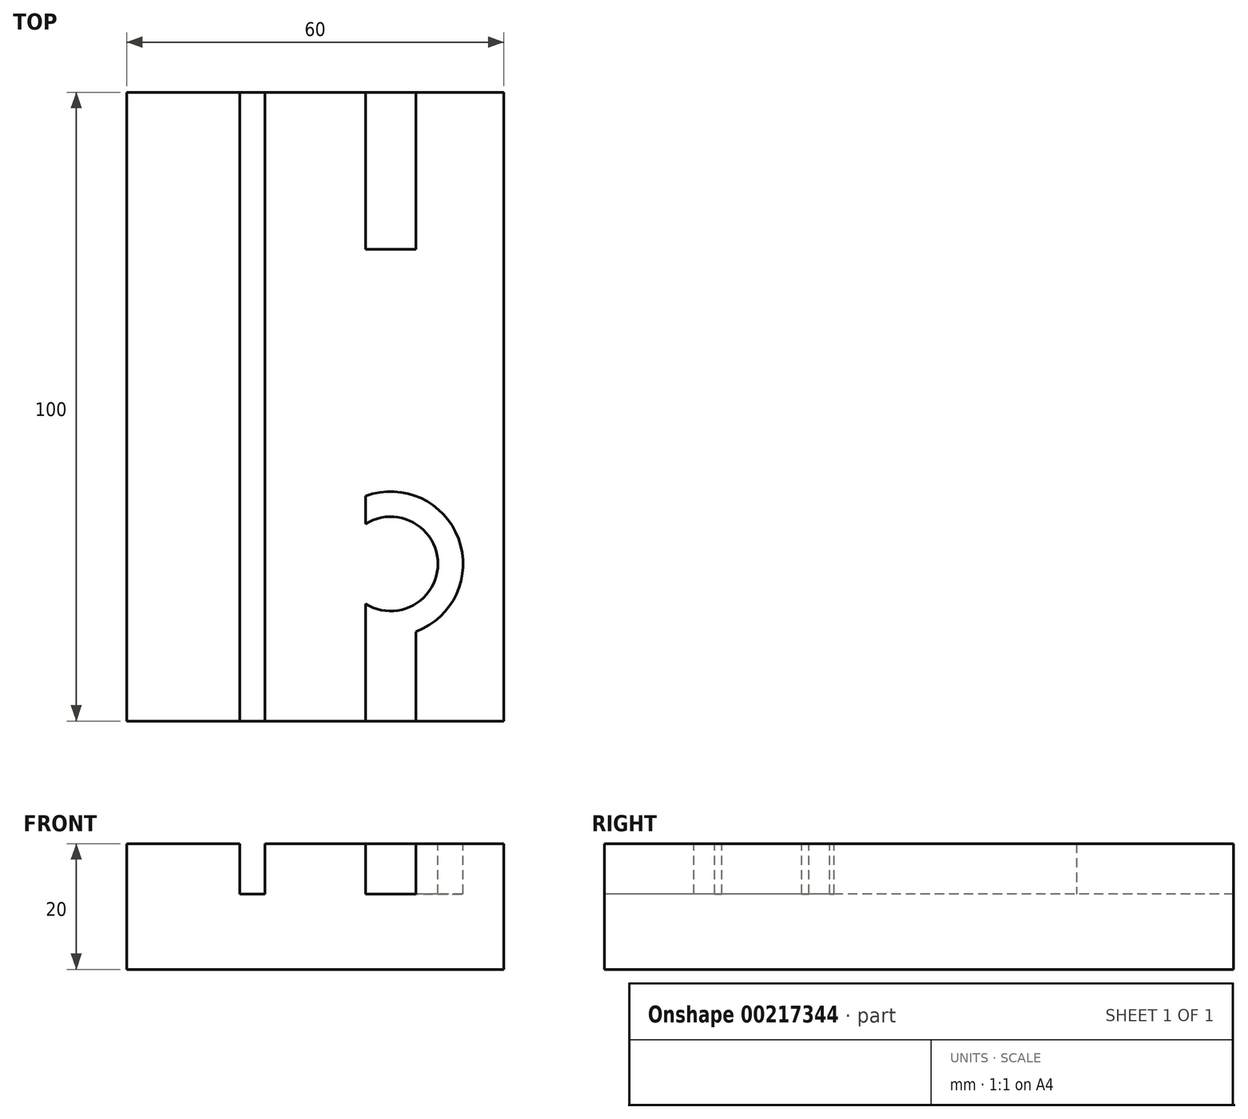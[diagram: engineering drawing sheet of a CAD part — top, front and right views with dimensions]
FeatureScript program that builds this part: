
annotation { "Feature Type Name" : "Feature", "Feature Type Description" : "" }
export const myFeature = defineFeature(function(context is Context, id is Id, definition is map)
    precondition{}
    {
        {
            var Q0;
            Q0=qCreatedBy(makeId("Top.planeOp"),FACE);
            var sketch = newSketch(context, id + "F0", { "sketchPlane" : qUnion([Q0])});
            skLineSegment(sketch, "E0.bottom", {"start": v(30, 50) * mm, "end": v(-30, 50) * mm});
            skLineSegment(sketch, "E0.top", {"start": v(30, -50) * mm, "end": v(-30, -50) * mm});
            skLineSegment(sketch, "E0.left", {"start": v(30, 50) * mm, "end": v(30, -50) * mm});
            skLineSegment(sketch, "E0.right", {"start": v(-30, 50) * mm, "end": v(-30, -50) * mm});
            skPoint(sketch, "E0.middle", {"position": v(0, 0) * mm});
            skSolve(sketch);
        }
        {
            var Q0;
            Q0=makeQuery(id+"F0.imprint","IMPRINT",FACE,{"disambiguationData":[TD([[makeQuery(id+"F0.imprint","IMPRINT",EDGE,{"derivedFrom":sQuery(id+"F0.wireOp",EDGE,"E0.bottom")}),1.0]])]});
            extrude(context, id + "F1", {"entities" : qUnion([Q0]), "endBound" : BoundingType.SYMMETRIC, "depth" : 20 * mm});
        }
        {
            var Q0;
            Q0=makeQuery(id+"F1.opExtrude","SWEPT_FACE",FACE,{"disambiguationData":[OSD([sQuery(id+"F0.wireOp",EDGE,"E0.top")])]});
            var sketch = newSketch(context, id + "F2", { "sketchPlane" : qUnion([Q0])});
            skLineSegment(sketch, "E1.bottom", {"start": v(-12, 10) * mm, "end": v(-8, 10) * mm});
            skLineSegment(sketch, "E1.top", {"start": v(-12, 2) * mm, "end": v(-8, 2) * mm});
            skLineSegment(sketch, "E1.left", {"start": v(-12, 10) * mm, "end": v(-12, 2) * mm});
            skLineSegment(sketch, "E1.right", {"start": v(-8, 10) * mm, "end": v(-8, 2) * mm});
            skLineSegment(sketch, "E2.bottom", {"start": v(8, 10) * mm, "end": v(16, 10) * mm});
            skLineSegment(sketch, "E2.top", {"start": v(8, 2) * mm, "end": v(16, 2) * mm});
            skLineSegment(sketch, "E2.left", {"start": v(8, 10) * mm, "end": v(8, 2) * mm});
            skLineSegment(sketch, "E2.right", {"start": v(16, 10) * mm, "end": v(16, 2) * mm});
            skSolve(sketch);
        }
        {
            var Q0;
            Q0=makeQuery(id+"F2.imprint","IMPRINT",FACE,{"disambiguationData":[TD([[makeQuery(id+"F2.imprint","IMPRINT",EDGE,{"derivedFrom":sQuery(id+"F2.wireOp",EDGE,"E1.bottom")}),1.0]])]});
            var Q1;
            Q1=makeQuery(id+"F2.imprint","IMPRINT",FACE,{"disambiguationData":[TD([[makeQuery(id+"F2.imprint","IMPRINT",EDGE,{"derivedFrom":sQuery(id+"F2.wireOp",EDGE,"c808f5a3-a914-4b55-8ba8-df2032bd41920.MirrorCS")}),1.0]])]});
            var Q2;
            Q2=makeQuery(id+"F2.imprint","IMPRINT",FACE,{"disambiguationData":[TD([[makeQuery(id+"F2.imprint","IMPRINT",EDGE,{"derivedFrom":sQuery(id+"F2.wireOp",EDGE,"E2.bottom")}),1.0]])]});
            extrude(context, id + "F3", {"entities" : qUnion([Q0, Q1, Q2]), "operationType" : NewBodyOperationType.REMOVE, "endBound" : BoundingType.THROUGH_ALL, "oppositeDirection" : true, "depth" : 25 * mm});
        }
        {
            var Q0;
            {var subQ0=sQuery(id+"F0.wireOp",EDGE,"E0.bottom");var subQ1=sQuery(id+"F0.wireOp",EDGE,"E0.top");Q0=makeQuery(id+"F3.boolean.opBoolean","SPLIT",FACE,{"disambiguationData":[TD([makeQuery(id+"F3.opExtrude","SWEPT_FACE",FACE,{"disambiguationData":[OSD([sQuery(id+"F2.wireOp",EDGE,"E1.right")])]})])],"derivedFrom":makeQuery(id+"F1.opExtrude","CAP_FACE",FACE,{"disambiguationData":[OSD([subQ0,subQ1,sQuery(id+"F0.wireOp",EDGE,"E0.left"),sQuery(id+"F0.wireOp",EDGE,"E0.right")])],"isStart":false})});}
            var sketch = newSketch(context, id + "F4", { "sketchPlane" : qUnion([Q0])});
            skSolve(sketch);
        }
        {
            var Q0;
            Q0=qCreatedBy(makeId("Front.planeOp"),FACE);
            var sketch = newSketch(context, id + "F5", { "sketchPlane" : qUnion([Q0])});
            skLineSegment(sketch, "E3.bottom", {"start": v(16, 10) * mm, "end": v(8, 10) * mm});
            skLineSegment(sketch, "E3.top", {"start": v(16, 2) * mm, "end": v(8, 2) * mm});
            skLineSegment(sketch, "E3.left", {"start": v(16, 10) * mm, "end": v(16, 2) * mm});
            skLineSegment(sketch, "E3.right", {"start": v(8, 10) * mm, "end": v(8, 2) * mm});
            skSolve(sketch);
        }
        {
            var Q0;
            Q0=makeQuery(id+"F5.imprint","IMPRINT",FACE,{"disambiguationData":[TD([[makeQuery(id+"F5.imprint","IMPRINT",EDGE,{"derivedFrom":sQuery(id+"F5.wireOp",EDGE,"E3.bottom")}),1.0]])]});
            extrude(context, id + "F6", {"entities" : qUnion([Q0]), "operationType" : NewBodyOperationType.ADD, "endBound" : BoundingType.SYMMETRIC, "depth" : 50 * mm});
        }
        {
            var Q0;
            {var subQ0=sQuery(id+"F2.wireOp",EDGE,"E1.right");var subQ1=sQuery(id+"F0.wireOp",EDGE,"E0.top");Q0=makeQuery(id+"F4.imprint","IMPRINT",FACE,{"disambiguationData":[TD([[makeQuery(id+"F4.imprint","IMPRINT",EDGE,{"derivedFrom":makeQuery(id+"F3.boolean.opBoolean","COPY",EDGE,{"derivedFrom":makeQuery(id+"F3.opExtrude","SWEPT_EDGE",EDGE,{"disambiguationData":[OSD([subQ1,sQuery(id+"F2.wireOp",EDGE,"E1.bottom"),subQ0])]})})}),1.0]])]});}
            var sketch = newSketch(context, id + "F7", { "sketchPlane" : qUnion([Q0])});
            skCircle(sketch, "E4", {"center": v(12, -25) * mm, "radius": 7.5 * mm});
            skCircle(sketch, "E5", {"center": v(12, -25) * mm, "radius": 11.5 * mm});
            skCircle(sketch, "E6.MirrorC", {"center": v(12, 25) * mm, "radius": 11.5 * mm});
            skCircle(sketch, "E7.MirrorC", {"center": v(12, 25) * mm, "radius": 7.5 * mm});
            skSolve(sketch);
        }
        {
            var Q0;
            {var subQ0=sQuery(id+"F7.wireOp",EDGE,"E6.MirrorC");var subQ1=makeQuery(id+"F4.imprint","IMPRINT",EDGE,{"derivedFrom":makeQuery(id+"F3.boolean.opBoolean","COPY",EDGE,{"derivedFrom":makeQuery(id+"F3.opExtrude","SWEPT_EDGE",EDGE,{"disambiguationData":[OSD([sQuery(id+"F0.wireOp",EDGE,"E0.top"),sQuery(id+"F2.wireOp",EDGE,"E2.bottom"),sQuery(id+"F2.wireOp",EDGE,"E2.left")])]})})});var subQ2=makeQuery(id+"F7.imprint","INTERSECT",VERTEX,{"disambiguationData":[OD(0.0)],"derivedFrom":[subQ1,subQ0]});Q0=makeQuery(id+"F7.imprint","IMPRINT",FACE,{"disambiguationData":[TD([[makeQuery(id+"F7.imprint","IMPRINT",EDGE,{"disambiguationData":[TD([[subQ2,-1.0]])],"derivedFrom":subQ0}),-1.0]])]});}
            var Q1;
            {var subQ0=sQuery(id+"F7.wireOp",EDGE,"E4");var subQ1=makeQuery(id+"F4.imprint","IMPRINT",EDGE,{"derivedFrom":makeQuery(id+"F3.boolean.opBoolean","COPY",EDGE,{"derivedFrom":makeQuery(id+"F3.opExtrude","SWEPT_EDGE",EDGE,{"disambiguationData":[OSD([sQuery(id+"F0.wireOp",EDGE,"E0.top"),sQuery(id+"F2.wireOp",EDGE,"E2.bottom"),sQuery(id+"F2.wireOp",EDGE,"E2.left")])]})})});var subQ2=makeQuery(id+"F7.imprint","INTERSECT",VERTEX,{"disambiguationData":[OD(0.0)],"derivedFrom":[subQ1,subQ0]});Q1=makeQuery(id+"F7.imprint","IMPRINT",FACE,{"disambiguationData":[TD([[makeQuery(id+"F7.imprint","IMPRINT",EDGE,{"disambiguationData":[TD([[subQ2,1.0]])],"derivedFrom":subQ0}),-1.0]])]});}
            var Q2;
            {var subQ0=sQuery(id+"F7.wireOp",EDGE,"E6.MirrorC");var subQ1=makeQuery(id+"F4.imprint","IMPRINT",EDGE,{"derivedFrom":makeQuery(id+"F3.boolean.opBoolean","COPY",EDGE,{"derivedFrom":makeQuery(id+"F3.opExtrude","SWEPT_EDGE",EDGE,{"disambiguationData":[OSD([sQuery(id+"F0.wireOp",EDGE,"E0.top"),sQuery(id+"F2.wireOp",EDGE,"E2.bottom"),sQuery(id+"F2.wireOp",EDGE,"E2.left")])]})})});var subQ2=makeQuery(id+"F7.imprint","INTERSECT",VERTEX,{"disambiguationData":[OD(0.0)],"derivedFrom":[subQ1,subQ0]});Q2=makeQuery(id+"F7.imprint","IMPRINT",FACE,{"disambiguationData":[TD([[makeQuery(id+"F7.imprint","IMPRINT",EDGE,{"disambiguationData":[TD([[subQ2,1.0]])],"derivedFrom":subQ0}),-1.0]])]});}
            var Q3;
            {var subQ0=sQuery(id+"F7.wireOp",EDGE,"E4");var subQ1=makeQuery(id+"F4.imprint","IMPRINT",EDGE,{"derivedFrom":makeQuery(id+"F3.boolean.opBoolean","COPY",EDGE,{"derivedFrom":makeQuery(id+"F3.opExtrude","SWEPT_EDGE",EDGE,{"disambiguationData":[OSD([sQuery(id+"F0.wireOp",EDGE,"E0.top"),sQuery(id+"F2.wireOp",EDGE,"E2.bottom"),sQuery(id+"F2.wireOp",EDGE,"E2.left")])]})})});var subQ2=makeQuery(id+"F7.imprint","INTERSECT",VERTEX,{"disambiguationData":[OD(0.0)],"derivedFrom":[subQ1,subQ0]});Q3=makeQuery(id+"F7.imprint","IMPRINT",FACE,{"disambiguationData":[TD([[makeQuery(id+"F7.imprint","IMPRINT",EDGE,{"disambiguationData":[TD([[subQ2,-1.0]])],"derivedFrom":subQ0}),-1.0]])]});}
            var Q4;
            Q4=makeQuery(id+"F6.boolean.opBoolean","SPLIT",FACE,{"disambiguationData":[TD([makeQuery(id+"F1.opExtrude","SWEPT_FACE",FACE,{"disambiguationData":[OSD([sQuery(id+"F0.wireOp",EDGE,"E0.top")])]})])],"derivedFrom":makeQuery(id+"F3.boolean.opBoolean","COPY",FACE,{"derivedFrom":makeQuery(id+"F3.opExtrude","SWEPT_FACE",FACE,{"disambiguationData":[OSD([sQuery(id+"F2.wireOp",EDGE,"E2.top")])]})})});
            extrude(context, id + "F8", {"entities" : qUnion([Q0, Q1, Q2, Q3]), "operationType" : NewBodyOperationType.REMOVE, "endBound" : BoundingType.UP_TO_SURFACE, "oppositeDirection" : true, "endBoundEntityFace" : qUnion([Q4]), "depth" : 25 * mm});
        }
        {
            var Q0;
            {var subQ0=sQuery(id+"F2.wireOp",EDGE,"E1.right");var subQ1=sQuery(id+"F0.wireOp",EDGE,"E0.top");Q0=makeQuery(id+"F4.imprint","IMPRINT",FACE,{"disambiguationData":[TD([[makeQuery(id+"F4.imprint","IMPRINT",EDGE,{"derivedFrom":makeQuery(id+"F3.boolean.opBoolean","COPY",EDGE,{"derivedFrom":makeQuery(id+"F3.opExtrude","SWEPT_EDGE",EDGE,{"disambiguationData":[OSD([subQ1,sQuery(id+"F2.wireOp",EDGE,"E1.bottom"),subQ0])]})})}),1.0]])]});}
            var sketch = newSketch(context, id + "F9", { "sketchPlane" : qUnion([Q0])});
            skCircle(sketch, "E8", {"center": v(12, -25) * mm, "radius": 7.5 * mm});
            skCircle(sketch, "E9.MirrorC", {"center": v(12, 25) * mm, "radius": 7.5 * mm});
            skSolve(sketch);
        }
        {
            var Q0;
            {var subQ0=sQuery(id+"F9.wireOp",EDGE,"E9.MirrorC");var subQ1=makeQuery(id+"F4.imprint","IMPRINT",EDGE,{"derivedFrom":makeQuery(id+"F3.boolean.opBoolean","COPY",EDGE,{"derivedFrom":makeQuery(id+"F3.opExtrude","SWEPT_EDGE",EDGE,{"disambiguationData":[OSD([sQuery(id+"F0.wireOp",EDGE,"E0.top"),sQuery(id+"F2.wireOp",EDGE,"E2.bottom"),sQuery(id+"F2.wireOp",EDGE,"E2.left")])]})})});var subQ2=makeQuery(id+"F9.imprint","INTERSECT",VERTEX,{"disambiguationData":[OD(0.0)],"derivedFrom":[subQ1,subQ0]});Q0=makeQuery(id+"F9.imprint","IMPRINT",FACE,{"disambiguationData":[TD([[makeQuery(id+"F9.imprint","IMPRINT",EDGE,{"disambiguationData":[TD([[subQ2,-1.0]])],"derivedFrom":subQ0}),-1.0]])]});}
            var Q1;
            {var subQ0=sQuery(id+"F9.wireOp",EDGE,"E8");var subQ1=makeQuery(id+"F4.imprint","IMPRINT",EDGE,{"derivedFrom":makeQuery(id+"F3.boolean.opBoolean","COPY",EDGE,{"derivedFrom":makeQuery(id+"F3.opExtrude","SWEPT_EDGE",EDGE,{"disambiguationData":[OSD([sQuery(id+"F0.wireOp",EDGE,"E0.top"),sQuery(id+"F2.wireOp",EDGE,"E2.bottom"),sQuery(id+"F2.wireOp",EDGE,"E2.left")])]})})});var subQ2=makeQuery(id+"F9.imprint","INTERSECT",VERTEX,{"disambiguationData":[OD(0.0)],"derivedFrom":[subQ1,subQ0]});Q1=makeQuery(id+"F9.imprint","IMPRINT",FACE,{"disambiguationData":[TD([[makeQuery(id+"F9.imprint","IMPRINT",EDGE,{"disambiguationData":[TD([[subQ2,-1.0]])],"derivedFrom":subQ0}),1.0]])]});}
            var Q2;
            Q2=makeQuery(id+"F8.boolean.opBoolean","MERGE",FACE,{"derivedFrom":[makeQuery(id+"F6.boolean.opBoolean","SPLIT",FACE,{"disambiguationData":[TD([makeQuery(id+"F1.opExtrude","SWEPT_FACE",FACE,{"disambiguationData":[OSD([sQuery(id+"F0.wireOp",EDGE,"E0.top")])]})])],"derivedFrom":makeQuery(id+"F3.boolean.opBoolean","COPY",FACE,{"derivedFrom":makeQuery(id+"F3.opExtrude","SWEPT_FACE",FACE,{"disambiguationData":[OSD([sQuery(id+"F2.wireOp",EDGE,"E2.top")])]})})}),makeQuery(id+"F8.opExtrude","CAP_FACE",FACE,{"disambiguationData":[OSD([sQuery(id+"F7.wireOp",EDGE,"E4"),sQuery(id+"F7.wireOp",EDGE,"E5")])],"isStart":false})]});
            extrude(context, id + "F10", {"entities" : qUnion([Q0, Q1]), "operationType" : NewBodyOperationType.ADD, "endBound" : BoundingType.UP_TO_SURFACE, "oppositeDirection" : true, "endBoundEntityFace" : qUnion([Q2]), "depth" : 25 * mm});
        }
    });
